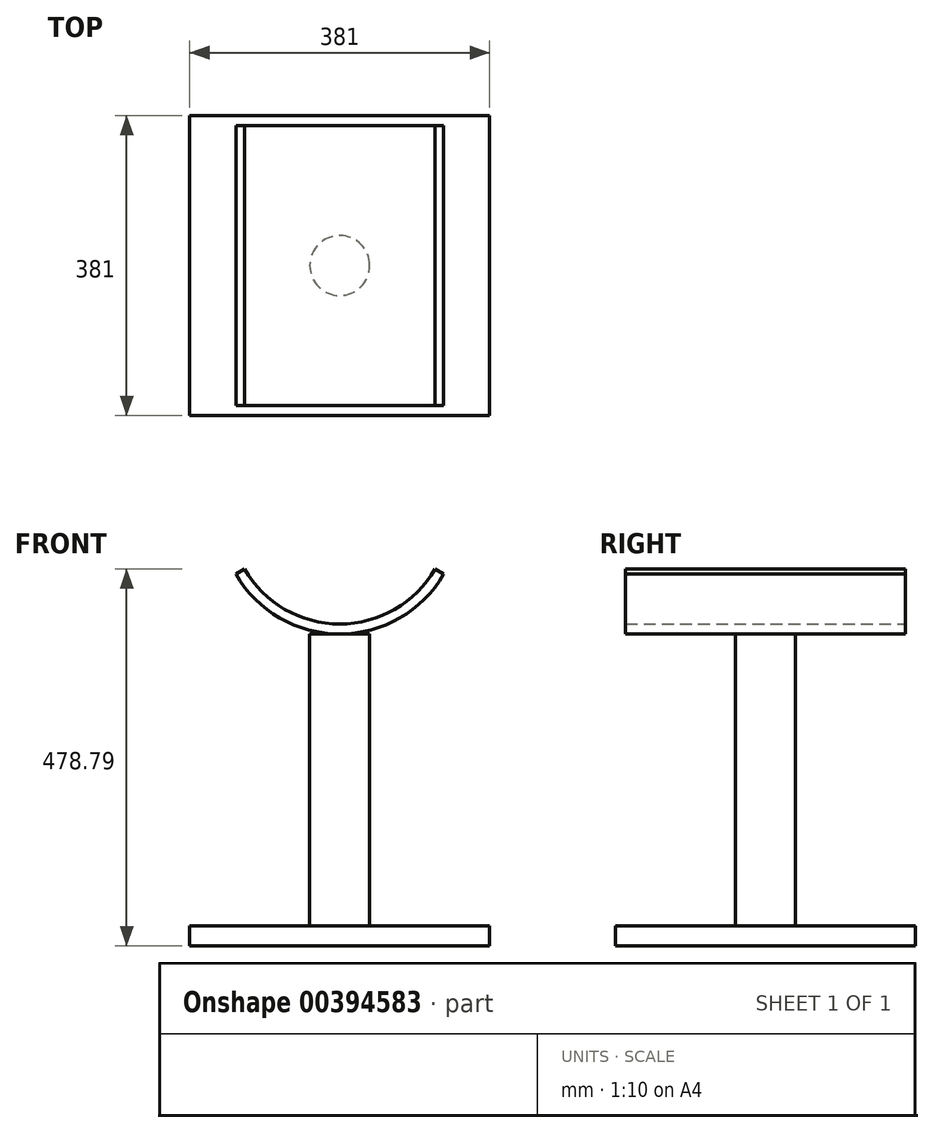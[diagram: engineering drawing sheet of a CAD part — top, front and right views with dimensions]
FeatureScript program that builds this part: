
annotation { "Feature Type Name" : "Feature", "Feature Type Description" : "" }
export const myFeature = defineFeature(function(context is Context, id is Id, definition is map)
    precondition{}
    {
        {
            var Q0;
            Q0=qCreatedBy(makeId("Top.planeOp"),FACE);
            var sketch = newSketch(context, id + "F0", { "sketchPlane" : qUnion([Q0])});
            skLineSegment(sketch, "E0.bottom", {"start": v(-190.5, 190.5) * mm, "end": v(190.5, 190.5) * mm});
            skLineSegment(sketch, "E0.top", {"start": v(-190.5, -190.5) * mm, "end": v(190.5, -190.5) * mm});
            skLineSegment(sketch, "E0.left", {"start": v(-190.5, 190.5) * mm, "end": v(-190.5, -190.5) * mm});
            skLineSegment(sketch, "E0.right", {"start": v(190.5, 190.5) * mm, "end": v(190.5, -190.5) * mm});
            skPoint(sketch, "E0.middle", {"position": v(0, 0) * mm});
            skSolve(sketch);
        }
        {
            var Q0;
            Q0=makeQuery(id+"F0.imprint","IMPRINT",FACE,{"disambiguationData":[TD([[makeQuery(id+"F0.imprint","IMPRINT",EDGE,{"derivedFrom":sQuery(id+"F0.wireOp",EDGE,"E0.bottom")}),-1.0]])]});
            extrude(context, id + "F1", {"entities" : qUnion([Q0]), "depth" : 25.4 * mm});
        }
        {
            var Q0;
            Q0=makeQuery(id+"F1.opExtrude","CAP_FACE",FACE,{"disambiguationData":[OSD([sQuery(id+"F0.wireOp",EDGE,"E0.bottom"),sQuery(id+"F0.wireOp",EDGE,"E0.top"),sQuery(id+"F0.wireOp",EDGE,"E0.left"),sQuery(id+"F0.wireOp",EDGE,"E0.right")])],"isStart":false});
            var sketch = newSketch(context, id + "F2", { "sketchPlane" : qUnion([Q0])});
            skCircle(sketch, "E1", {"center": v(0, 0) * mm, "radius": 38.1 * mm});
            skSolve(sketch);
        }
        {
            var Q0;
            Q0=makeQuery(id+"F2.imprint","IMPRINT",FACE,{"disambiguationData":[TD([[makeQuery(id+"F2.imprint","IMPRINT",EDGE,{"derivedFrom":sQuery(id+"F2.wireOp",EDGE,"E1")}),1.0]])]});
            var Q1;
            Q1=sQuery(id+"F2.wireOp",EDGE,"3UVDaw8X-qVf4-TKE0-4b5v-L4qAUtcxqyn6");
            extrude(context, id + "F3", {"entities" : qUnion([Q0]), "surfaceEntities" : qUnion([Q1]), "depth" : 370.84 * mm});
        }
        {
            var Q0;
            Q0=qCreatedBy(makeId("Front.planeOp"),FACE);
            var sketch = newSketch(context, id + "F4", { "sketchPlane" : qUnion([Q0])});
            skArc(sketch, "E2", {"start": v(-131.98, 472.44) * mm, "mid": v(0, 396.24) * mm, "end": v(131.98, 472.44) * mm});
            skLineSegment(sketch, "E3", {"start": v(0, 548.64) * mm, "end": v(0, 701.04) * mm, "construction": true});
            skLineSegment(sketch, "E4", {"start": v(0, 548.64) * mm, "end": v(-131.98, 472.44) * mm, "construction": true});
            skArc(sketch, "E5.0", {"start": v(-120.98, 478.8) * mm, "mid": v(0, 408.94) * mm, "end": v(120.98, 478.8) * mm});
            skLineSegment(sketch, "E6", {"start": v(131.98, 472.44) * mm, "end": v(120.98, 478.8) * mm});
            skLineSegment(sketch, "E7", {"start": v(-131.98, 472.44) * mm, "end": v(-120.98, 478.8) * mm});
            skSolve(sketch);
        }
        {
            var Q0;
            Q0 = qSketchRegion(id + "F4", true);
            extrude(context, id + "F5", {"entities" : qUnion([Q0]), "endBound" : BoundingType.SYMMETRIC, "depth" : 355.6 * mm});
        }
    });
